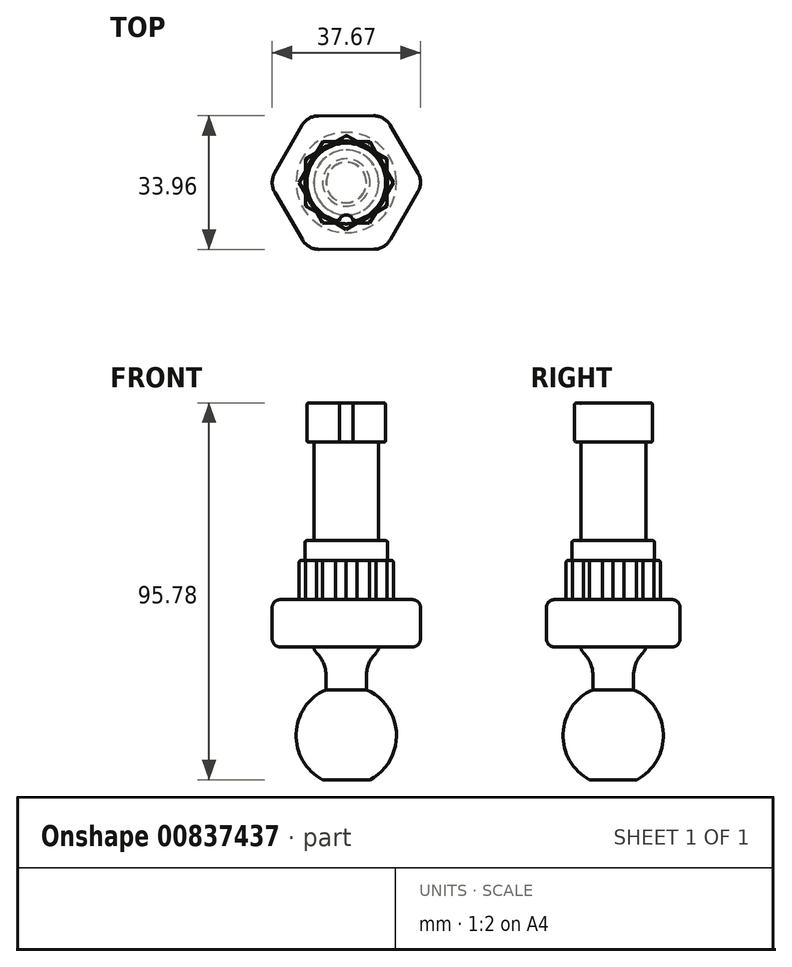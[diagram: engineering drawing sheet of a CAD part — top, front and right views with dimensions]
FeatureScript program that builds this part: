
annotation { "Feature Type Name" : "Feature", "Feature Type Description" : "" }
export const myFeature = defineFeature(function(context is Context, id is Id, definition is map)
    precondition{}
    {
        {
            var Q0;
            Q0=qCreatedBy(makeId("Top.planeOp"),FACE);
            var sketch = newSketch(context, id + "F0", { "sketchPlane" : qUnion([Q0])});
            skCircle(sketch, "E0.cCircle", {"center": v(0, 0) * mm, "radius": 11.95 * mm, "construction": true});
            skLineSegment(sketch, "E0.0", {"start": v(10.36, 5.96) * mm, "end": v(10.36, 2.75) * mm});
            skLineSegment(sketch, "E0.1", {"start": v(10.34, -6) * mm, "end": v(7.56, -7.6) * mm});
            skLineSegment(sketch, "E0.2", {"start": v(-0.02, -11.95) * mm, "end": v(-2.8, -10.34) * mm});
            skLineSegment(sketch, "E0.3", {"start": v(-10.36, -5.96) * mm, "end": v(-10.36, -2.75) * mm});
            skLineSegment(sketch, "E0.4", {"start": v(-10.34, 6) * mm, "end": v(-7.56, 7.6) * mm});
            skLineSegment(sketch, "E0.5", {"start": v(0.02, 11.95) * mm, "end": v(2.8, 10.34) * mm});
            skLineSegment(sketch, "E1", {"start": v(6, 10.34) * mm, "end": v(6.72, 11.59) * mm, "construction": true});
            skLineSegment(sketch, "E2.0", {"start": v(6, 10.34) * mm, "end": v(7.6, 7.56) * mm});
            skLineSegment(sketch, "E2.1", {"start": v(11.95, -0.02) * mm, "end": v(10.34, -2.8) * mm});
            skLineSegment(sketch, "E2.2", {"start": v(5.96, -10.36) * mm, "end": v(2.75, -10.36) * mm});
            skLineSegment(sketch, "E2.3", {"start": v(-6, -10.34) * mm, "end": v(-7.6, -7.56) * mm});
            skLineSegment(sketch, "E2.4", {"start": v(-11.95, 0.02) * mm, "end": v(-10.34, 2.8) * mm});
            skLineSegment(sketch, "E2.5", {"start": v(-5.96, 10.36) * mm, "end": v(-2.75, 10.36) * mm});
            skLineSegment(sketch, "E3.trimOffspring", {"start": v(-7.6, -7.56) * mm, "end": v(-10.36, -5.96) * mm});
            skPoint(sketch, "E4.orphan", {"position": v(-5.2, -8.95) * mm});
            skLineSegment(sketch, "E5.trimOffspring", {"start": v(-10.36, -2.75) * mm, "end": v(-11.95, 0.02) * mm});
            skLineSegment(sketch, "E6.trimOffspring", {"start": v(-2.8, -10.34) * mm, "end": v(-6, -10.34) * mm});
            skLineSegment(sketch, "E7.trimOffspring", {"start": v(2.75, -10.36) * mm, "end": v(-0.02, -11.95) * mm});
            skLineSegment(sketch, "E8.trimOffspring", {"start": v(7.56, -7.6) * mm, "end": v(5.96, -10.36) * mm});
            skLineSegment(sketch, "E9.trimOffspring", {"start": v(-10.34, 2.8) * mm, "end": v(-10.34, 6) * mm});
            skLineSegment(sketch, "E10.trimOffspring", {"start": v(-7.56, 7.6) * mm, "end": v(-5.96, 10.36) * mm});
            skLineSegment(sketch, "E11.trimOffspring", {"start": v(-2.75, 10.36) * mm, "end": v(0.02, 11.95) * mm});
            skLineSegment(sketch, "E12.trimOffspring", {"start": v(2.8, 10.34) * mm, "end": v(6, 10.34) * mm});
            skLineSegment(sketch, "E13.trimOffspring", {"start": v(7.6, 7.56) * mm, "end": v(10.36, 5.96) * mm});
            skPoint(sketch, "E14.orphan", {"position": v(5.2, 8.95) * mm});
            skLineSegment(sketch, "E15.trimOffspring", {"start": v(10.36, 2.75) * mm, "end": v(11.95, -0.02) * mm});
            skLineSegment(sketch, "E16.trimOffspring", {"start": v(10.34, -2.8) * mm, "end": v(10.34, -6) * mm});
            skSolve(sketch);
        }
        {
            var Q0;
            Q0=makeQuery(id+"F0.imprint","IMPRINT",FACE,{"disambiguationData":[TD([[makeQuery(id+"F0.imprint","IMPRINT",EDGE,{"derivedFrom":sQuery(id+"F0.wireOp",EDGE,"E0.0")}),-1.0]])]});
            extrude(context, id + "F1", {"entities" : qUnion([Q0]), "depth" : 10 * mm, "offsetDistance" : 25 * mm});
        }
        {
            var Q0;
            Q0=makeQuery(id+"F1.opExtrude","CAP_FACE",FACE,{"disambiguationData":[OSD([sQuery(id+"F0.wireOp",EDGE,"E0.0"),sQuery(id+"F0.wireOp",EDGE,"E0.1"),sQuery(id+"F0.wireOp",EDGE,"E0.2"),sQuery(id+"F0.wireOp",EDGE,"E0.3"),sQuery(id+"F0.wireOp",EDGE,"E0.4"),sQuery(id+"F0.wireOp",EDGE,"E0.5"),sQuery(id+"F0.wireOp",EDGE,"E2.0"),sQuery(id+"F0.wireOp",EDGE,"E2.1"),sQuery(id+"F0.wireOp",EDGE,"E2.2"),sQuery(id+"F0.wireOp",EDGE,"E2.3"),sQuery(id+"F0.wireOp",EDGE,"E2.4"),sQuery(id+"F0.wireOp",EDGE,"E2.5"),sQuery(id+"F0.wireOp",EDGE,"E3.trimOffspring"),sQuery(id+"F0.wireOp",EDGE,"E5.trimOffspring"),sQuery(id+"F0.wireOp",EDGE,"E6.trimOffspring"),sQuery(id+"F0.wireOp",EDGE,"E7.trimOffspring"),sQuery(id+"F0.wireOp",EDGE,"E8.trimOffspring"),sQuery(id+"F0.wireOp",EDGE,"E9.trimOffspring"),sQuery(id+"F0.wireOp",EDGE,"E10.trimOffspring"),sQuery(id+"F0.wireOp",EDGE,"E11.trimOffspring"),sQuery(id+"F0.wireOp",EDGE,"E12.trimOffspring"),sQuery(id+"F0.wireOp",EDGE,"E13.trimOffspring"),sQuery(id+"F0.wireOp",EDGE,"E15.trimOffspring"),sQuery(id+"F0.wireOp",EDGE,"E16.trimOffspring")])],"isStart":false});
            var sketch = newSketch(context, id + "F2", { "sketchPlane" : qUnion([Q0])});
            skLineSegment(sketch, "E17", {"start": v(-10.36, -2.75) * mm, "end": v(10.36, 2.75) * mm, "construction": true});
            skLineSegment(sketch, "E18", {"start": v(2.75, -10.36) * mm, "end": v(-2.75, 10.36) * mm, "construction": true});
            skCircle(sketch, "E19", {"center": v(0, 0) * mm, "radius": 10.5 * mm});
            skSolve(sketch);
        }
        {
            var Q0;
            Q0=makeQuery(id+"F2.imprint","IMPRINT",FACE,{"disambiguationData":[TD([[makeQuery(id+"F2.imprint","IMPRINT",EDGE,{"derivedFrom":sQuery(id+"F2.wireOp",EDGE,"E19")}),1.0]])]});
            extrude(context, id + "F3", {"entities" : qUnion([Q0]), "operationType" : NewBodyOperationType.ADD, "depth" : 5 * mm, "offsetDistance" : 25 * mm});
        }
        {
            var Q0;
            Q0=makeQuery(id+"F1.opExtrude","CAP_EDGE",EDGE,{"disambiguationData":[OSD([sQuery(id+"F0.wireOp",EDGE,"E2.5")])],"isStart":false});
            var Q1;
            Q1=makeQuery(id+"F1.opExtrude","CAP_EDGE",EDGE,{"disambiguationData":[OSD([sQuery(id+"F0.wireOp",EDGE,"E10.trimOffspring")])],"isStart":false});
            var Q2;
            Q2=makeQuery(id+"F1.opExtrude","CAP_EDGE",EDGE,{"disambiguationData":[OSD([sQuery(id+"F0.wireOp",EDGE,"E0.4")])],"isStart":false});
            var Q3;
            Q3=makeQuery(id+"F1.opExtrude","CAP_EDGE",EDGE,{"disambiguationData":[OSD([sQuery(id+"F0.wireOp",EDGE,"E9.trimOffspring")])],"isStart":false});
            var Q4;
            Q4=makeQuery(id+"F1.opExtrude","CAP_EDGE",EDGE,{"disambiguationData":[OSD([sQuery(id+"F0.wireOp",EDGE,"E2.4")])],"isStart":false});
            var Q5;
            Q5=makeQuery(id+"F1.opExtrude","CAP_EDGE",EDGE,{"disambiguationData":[OSD([sQuery(id+"F0.wireOp",EDGE,"E5.trimOffspring")])],"isStart":false});
            var Q6;
            Q6=makeQuery(id+"F1.opExtrude","CAP_EDGE",EDGE,{"disambiguationData":[OSD([sQuery(id+"F0.wireOp",EDGE,"E0.3")])],"isStart":false});
            var Q7;
            Q7=makeQuery(id+"F1.opExtrude","CAP_EDGE",EDGE,{"disambiguationData":[OSD([sQuery(id+"F0.wireOp",EDGE,"E3.trimOffspring")])],"isStart":false});
            var Q8;
            Q8=makeQuery(id+"F1.opExtrude","CAP_EDGE",EDGE,{"disambiguationData":[OSD([sQuery(id+"F0.wireOp",EDGE,"E2.3")])],"isStart":false});
            var Q9;
            Q9=makeQuery(id+"F1.opExtrude","CAP_EDGE",EDGE,{"disambiguationData":[OSD([sQuery(id+"F0.wireOp",EDGE,"E6.trimOffspring")])],"isStart":false});
            var Q10;
            Q10=makeQuery(id+"F1.opExtrude","CAP_EDGE",EDGE,{"disambiguationData":[OSD([sQuery(id+"F0.wireOp",EDGE,"E0.2")])],"isStart":false});
            var Q11;
            Q11=makeQuery(id+"F1.opExtrude","CAP_EDGE",EDGE,{"disambiguationData":[OSD([sQuery(id+"F0.wireOp",EDGE,"E7.trimOffspring")])],"isStart":false});
            var Q12;
            Q12=makeQuery(id+"F1.opExtrude","CAP_EDGE",EDGE,{"disambiguationData":[OSD([sQuery(id+"F0.wireOp",EDGE,"E2.2")])],"isStart":false});
            var Q13;
            Q13=makeQuery(id+"F1.opExtrude","CAP_EDGE",EDGE,{"disambiguationData":[OSD([sQuery(id+"F0.wireOp",EDGE,"E8.trimOffspring")])],"isStart":false});
            var Q14;
            Q14=makeQuery(id+"F1.opExtrude","CAP_EDGE",EDGE,{"disambiguationData":[OSD([sQuery(id+"F0.wireOp",EDGE,"E0.1")])],"isStart":false});
            var Q15;
            Q15=makeQuery(id+"F1.opExtrude","CAP_EDGE",EDGE,{"disambiguationData":[OSD([sQuery(id+"F0.wireOp",EDGE,"E16.trimOffspring")])],"isStart":false});
            var Q16;
            Q16=makeQuery(id+"F1.opExtrude","CAP_EDGE",EDGE,{"disambiguationData":[OSD([sQuery(id+"F0.wireOp",EDGE,"E2.1")])],"isStart":false});
            var Q17;
            Q17=makeQuery(id+"F1.opExtrude","CAP_EDGE",EDGE,{"disambiguationData":[OSD([sQuery(id+"F0.wireOp",EDGE,"E15.trimOffspring")])],"isStart":false});
            var Q18;
            Q18=makeQuery(id+"F1.opExtrude","CAP_EDGE",EDGE,{"disambiguationData":[OSD([sQuery(id+"F0.wireOp",EDGE,"E0.0")])],"isStart":false});
            var Q19;
            Q19=makeQuery(id+"F1.opExtrude","CAP_EDGE",EDGE,{"disambiguationData":[OSD([sQuery(id+"F0.wireOp",EDGE,"E13.trimOffspring")])],"isStart":false});
            var Q20;
            Q20=makeQuery(id+"F1.opExtrude","CAP_EDGE",EDGE,{"disambiguationData":[OSD([sQuery(id+"F0.wireOp",EDGE,"E2.0")])],"isStart":false});
            var Q21;
            Q21=makeQuery(id+"F1.opExtrude","CAP_EDGE",EDGE,{"disambiguationData":[OSD([sQuery(id+"F0.wireOp",EDGE,"E12.trimOffspring")])],"isStart":false});
            var Q22;
            Q22=makeQuery(id+"F1.opExtrude","CAP_EDGE",EDGE,{"disambiguationData":[OSD([sQuery(id+"F0.wireOp",EDGE,"E0.5")])],"isStart":false});
            var Q23;
            Q23=makeQuery(id+"F1.opExtrude","CAP_EDGE",EDGE,{"disambiguationData":[OSD([sQuery(id+"F0.wireOp",EDGE,"E11.trimOffspring")])],"isStart":false});
            fillet(context, id + "F4", {"entities" : qUnion([Q0, Q1, Q2, Q3, Q4, Q5, Q6, Q7, Q8, Q9, Q10, Q11, Q12, Q13, Q14, Q15, Q16, Q17, Q18, Q19, Q20, Q21, Q22, Q23]), "radius" : .5 * mm, "tangentPropagation" : true, "allowEdgeOverflow" : false});
        }
        {
            var Q0;
            Q0=makeQuery(id+"F3.opExtrude","CAP_FACE",FACE,{"disambiguationData":[OSD([sQuery(id+"F2.wireOp",EDGE,"E19")])],"isStart":false});
            var sketch = newSketch(context, id + "F5", { "sketchPlane" : qUnion([Q0])});
            skCircle(sketch, "E20", {"center": v(0, 0) * mm, "radius": 8.25 * mm});
            skSolve(sketch);
        }
        {
            var Q0;
            Q0=makeQuery(id+"F5.imprint","IMPRINT",FACE,{"disambiguationData":[TD([[makeQuery(id+"F5.imprint","IMPRINT",EDGE,{"derivedFrom":sQuery(id+"F5.wireOp",EDGE,"E20")}),1.0]])]});
            extrude(context, id + "F6", {"entities" : qUnion([Q0]), "operationType" : NewBodyOperationType.ADD, "depth" : 25 * mm, "offsetDistance" : 25 * mm});
        }
        {
            var Q0;
            Q0=makeQuery(id+"F6.opExtrude","CAP_FACE",FACE,{"disambiguationData":[OSD([sQuery(id+"F5.wireOp",EDGE,"E20")])],"isStart":false});
            var sketch = newSketch(context, id + "F7", { "sketchPlane" : qUnion([Q0])});
            skCircle(sketch, "E21", {"center": v(0, 0) * mm, "radius": 10 * mm});
            skSolve(sketch);
        }
        {
            var Q0;
            Q0=makeQuery(id+"F7.imprint","IMPRINT",FACE,{"disambiguationData":[TD([[makeQuery(id+"F7.imprint","IMPRINT",EDGE,{"derivedFrom":sQuery(id+"F7.wireOp",EDGE,"E21")}),1.0]])]});
            var Q1;
            Q1=makeQuery(id+"F7.imprint","IMPRINT",FACE,{"disambiguationData":[TD([[makeQuery(id+"F7.imprint","IMPRINT",EDGE,{"derivedFrom":makeQuery(id+"F6.opExtrude","CAP_EDGE",EDGE,{"disambiguationData":[OSD([sQuery(id+"F5.wireOp",EDGE,"E20")])],"isStart":false})}),1.0]])]});
            extrude(context, id + "F8", {"entities" : qUnion([Q0, Q1]), "operationType" : NewBodyOperationType.ADD, "depth" : 10 * mm, "offsetDistance" : 25 * mm});
        }
        {
            var Q0;
            Q0=makeQuery(id+"F8.opExtrude","CAP_FACE",FACE,{"disambiguationData":[OSD([sQuery(id+"F7.wireOp",EDGE,"E21")])],"isStart":true});
            var sketch = newSketch(context, id + "F9", { "sketchPlane" : qUnion([Q0])});
            skLineSegment(sketch, "E22", {"start": v(0, 10) * mm, "end": v(0, 8.25) * mm, "construction": true});
            skArc(sketch, "E23", {"start": v(0, 8.25) * mm, "mid": v(1.18, 8.7) * mm, "end": v(1.74, 9.85) * mm});
            skArc(sketch, "E24", {"start": v(0, 8.25) * mm, "mid": v(-1.18, 8.7) * mm, "end": v(-1.74, 9.85) * mm});
            skSolve(sketch);
        }
        {
            var Q0;
            {var subQ0=sQuery(id+"F9.wireOp",EDGE,"E23");Q0=makeQuery(id+"F9.imprint","IMPRINT",FACE,{"disambiguationData":[TD([[makeQuery(id+"F9.imprint","IMPRINT",EDGE,{"derivedFrom":subQ0}),1.0]])]});}
            extrude(context, id + "F10", {"entities" : qUnion([Q0]), "operationType" : NewBodyOperationType.REMOVE, "oppositeDirection" : true, "depth" : 25 * mm, "offsetDistance" : 25 * mm});
        }
        {
            var Q0;
            Q0=makeQuery(id+"F8.opExtrude","CAP_EDGE",EDGE,{"disambiguationData":[OSD([sQuery(id+"F7.wireOp",EDGE,"E21")])],"isStart":false});
            var Q1;
            Q1=makeQuery(id+"F10.boolean.opBoolean","INTERSECT",EDGE,{"derivedFrom":[makeQuery(id+"F8.opExtrude","CAP_FACE",FACE,{"disambiguationData":[OSD([sQuery(id+"F7.wireOp",EDGE,"E21")])],"isStart":false}),makeQuery(id+"F10.opExtrude","SWEPT_FACE",FACE,{"disambiguationData":[OSD([sQuery(id+"F9.wireOp",EDGE,"E23"),sQuery(id+"F9.wireOp",EDGE,"E24")])]})]});
            var Q2;
            Q2=makeQuery(id+"F10.boolean.opBoolean","COPY",EDGE,{"derivedFrom":makeQuery(id+"F10.opExtrude","SWEPT_EDGE",EDGE,{"disambiguationData":[OSD([sQuery(id+"F7.wireOp",EDGE,"E21"),sQuery(id+"F9.wireOp",EDGE,"E24")])]})});
            var Q3;
            Q3=makeQuery(id+"F10.boolean.opBoolean","COPY",EDGE,{"derivedFrom":makeQuery(id+"F10.opExtrude","SWEPT_EDGE",EDGE,{"disambiguationData":[OSD([sQuery(id+"F7.wireOp",EDGE,"E21"),sQuery(id+"F9.wireOp",EDGE,"E23")])]})});
            var Q4;
            Q4=makeQuery(id+"F8.opExtrude","CAP_EDGE",EDGE,{"disambiguationData":[OSD([sQuery(id+"F7.wireOp",EDGE,"E21")])],"isStart":true});
            var Q5;
            Q5=makeQuery(id+"F10.boolean.opBoolean","COPY",EDGE,{"disambiguationData":[OD(1.0)],"derivedFrom":makeQuery(id+"F10.opExtrude","CAP_EDGE",EDGE,{"disambiguationData":[OSD([sQuery(id+"F9.wireOp",EDGE,"E23"),sQuery(id+"F9.wireOp",EDGE,"E24")])],"isStart":true})});
            var Q6;
            Q6=makeQuery(id+"F10.boolean.opBoolean","COPY",EDGE,{"disambiguationData":[OD(0.0)],"derivedFrom":makeQuery(id+"F10.opExtrude","CAP_EDGE",EDGE,{"disambiguationData":[OSD([sQuery(id+"F9.wireOp",EDGE,"E23"),sQuery(id+"F9.wireOp",EDGE,"E24")])],"isStart":true})});
            fillet(context, id + "F11", {"entities" : qUnion([Q0, Q1, Q2, Q3, Q4, Q5, Q6]), "radius" : .5 * mm, "tangentPropagation" : true, "allowEdgeOverflow" : false});
        }
        {
            var Q0;
            Q0=makeQuery(id+"F6.opExtrude","CAP_EDGE",EDGE,{"disambiguationData":[OSD([sQuery(id+"F5.wireOp",EDGE,"E20")])],"isStart":true});
            var Q1;
            Q1=makeQuery(id+"F3.opExtrude","CAP_EDGE",EDGE,{"disambiguationData":[OSD([sQuery(id+"F2.wireOp",EDGE,"E19")])],"isStart":false});
            fillet(context, id + "F12", {"entities" : qUnion([Q0, Q1]), "radius" : .5 * mm, "tangentPropagation" : true, "allowEdgeOverflow" : false});
        }
        {
            var Q0;
            Q0=makeQuery(id+"F1.opExtrude","CAP_FACE",FACE,{"disambiguationData":[OSD([sQuery(id+"F0.wireOp",EDGE,"E0.0"),sQuery(id+"F0.wireOp",EDGE,"E0.1"),sQuery(id+"F0.wireOp",EDGE,"E0.2"),sQuery(id+"F0.wireOp",EDGE,"E0.3"),sQuery(id+"F0.wireOp",EDGE,"E0.4"),sQuery(id+"F0.wireOp",EDGE,"E0.5"),sQuery(id+"F0.wireOp",EDGE,"E2.0"),sQuery(id+"F0.wireOp",EDGE,"E2.1"),sQuery(id+"F0.wireOp",EDGE,"E2.2"),sQuery(id+"F0.wireOp",EDGE,"E2.3"),sQuery(id+"F0.wireOp",EDGE,"E2.4"),sQuery(id+"F0.wireOp",EDGE,"E2.5"),sQuery(id+"F0.wireOp",EDGE,"E3.trimOffspring"),sQuery(id+"F0.wireOp",EDGE,"E5.trimOffspring"),sQuery(id+"F0.wireOp",EDGE,"E6.trimOffspring"),sQuery(id+"F0.wireOp",EDGE,"E7.trimOffspring"),sQuery(id+"F0.wireOp",EDGE,"E8.trimOffspring"),sQuery(id+"F0.wireOp",EDGE,"E9.trimOffspring"),sQuery(id+"F0.wireOp",EDGE,"E10.trimOffspring"),sQuery(id+"F0.wireOp",EDGE,"E11.trimOffspring"),sQuery(id+"F0.wireOp",EDGE,"E12.trimOffspring"),sQuery(id+"F0.wireOp",EDGE,"E13.trimOffspring"),sQuery(id+"F0.wireOp",EDGE,"E15.trimOffspring"),sQuery(id+"F0.wireOp",EDGE,"E16.trimOffspring")])],"isStart":true});
            var sketch = newSketch(context, id + "F13", { "sketchPlane" : qUnion([Q0])});
            skCircle(sketch, "E25.cCircle", {"center": v(0, 0) * mm, "radius": 16.96 * mm, "construction": true});
            skLineSegment(sketch, "E25.0", {"start": v(-11.22, -14.53) * mm, "end": v(-18.17, -2.4) * mm});
            skLineSegment(sketch, "E25.1", {"start": v(-18.16, 2.5) * mm, "end": v(-11.17, 14.54) * mm});
            skLineSegment(sketch, "E25.2", {"start": v(-6.92, 16.98) * mm, "end": v(7.06, 16.94) * mm});
            skLineSegment(sketch, "E25.3", {"start": v(11.22, 14.53) * mm, "end": v(18.2, 2.35) * mm});
            skLineSegment(sketch, "E25.4", {"start": v(18.2, -2.45) * mm, "end": v(11.17, -14.54) * mm});
            skLineSegment(sketch, "E25.5", {"start": v(6.92, -16.98) * mm, "end": v(-7.06, -16.94) * mm});
            skPoint(sketch, "E25.0.midPoint", {"position": v(-14.7, -8.44) * mm});
            skPoint(sketch, "E26.visualSharp", {"position": v(9.75, -16.99) * mm});
            skArc(sketch, "E26.filletArc", {"start": v(6.92, -16.98) * mm, "mid": v(9.37, -16.33) * mm, "end": v(11.17, -14.54) * mm});
            skPoint(sketch, "E27.visualSharp", {"position": v(-9.84, -16.93) * mm});
            skArc(sketch, "E27.filletArc", {"start": v(-11.22, -14.53) * mm, "mid": v(-9.46, -16.3) * mm, "end": v(-7.06, -16.94) * mm});
            skPoint(sketch, "E28.visualSharp", {"position": v(-19.58, 0.05) * mm});
            skArc(sketch, "E28.filletArc", {"start": v(-18.16, 2.5) * mm, "mid": v(-18.82, 0.05) * mm, "end": v(-18.17, -2.4) * mm});
            skPoint(sketch, "E29.visualSharp", {"position": v(-9.75, 16.99) * mm});
            skArc(sketch, "E29.filletArc", {"start": v(-6.92, 16.98) * mm, "mid": v(-9.37, 16.33) * mm, "end": v(-11.17, 14.54) * mm});
            skPoint(sketch, "E30.visualSharp", {"position": v(9.84, 16.93) * mm});
            skArc(sketch, "E30.filletArc", {"start": v(11.22, 14.53) * mm, "mid": v(9.46, 16.3) * mm, "end": v(7.06, 16.94) * mm});
            skPoint(sketch, "E31.visualSharp", {"position": v(19.58, -0.05) * mm});
            skArc(sketch, "E31.filletArc", {"start": v(18.2, -2.45) * mm, "mid": v(18.84, -0.05) * mm, "end": v(18.2, 2.35) * mm});
            skSolve(sketch);
        }
        {
            var Q0;
            Q0=makeQuery(id+"F13.imprint","IMPRINT",FACE,{"disambiguationData":[TD([[makeQuery(id+"F13.imprint","IMPRINT",EDGE,{"derivedFrom":sQuery(id+"F13.wireOp",EDGE,"XwkZxwQT-tXsu-qyU6-IrZG-78iqKTn2pKXx")}),1.0]])]});
            var Q1;
            Q1=makeQuery(id+"F13.imprint","IMPRINT",FACE,{"disambiguationData":[TD([[makeQuery(id+"F13.imprint","IMPRINT",EDGE,{"derivedFrom":makeQuery(id+"F1.opExtrude","CAP_EDGE",EDGE,{"disambiguationData":[OSD([sQuery(id+"F0.wireOp",EDGE,"E0.0")])],"isStart":true})}),1.0]])]});
            var Q2;
            Q2=makeQuery(id+"F13.imprint","IMPRINT",FACE,{"disambiguationData":[TD([[makeQuery(id+"F13.imprint","IMPRINT",EDGE,{"derivedFrom":sQuery(id+"F13.wireOp",EDGE,"E25.0")}),-1.0]])]});
            extrude(context, id + "F14", {"entities" : qUnion([Q0, Q1, Q2]), "operationType" : NewBodyOperationType.ADD, "depth" : 12 * mm, "offsetDistance" : 25 * mm});
        }
        {
            var Q0;
            Q0=makeQuery(id+"F14.opExtrude","CAP_EDGE",EDGE,{"disambiguationData":[OSD([sQuery(id+"F13.wireOp",EDGE,"XwkZxwQT-tXsu-qyU6-IrZG-78iqKTn2pKXx")])],"isStart":false});
            var Q1;
            Q1=makeQuery(id+"F14.opExtrude","CAP_EDGE",EDGE,{"disambiguationData":[OSD([sQuery(id+"F13.wireOp",EDGE,"XwkZxwQT-tXsu-qyU6-IrZG-78iqKTn2pKXx")])],"isStart":true});
            var Q2;
            Q2=makeQuery(id+"F14.opExtrude","CAP_EDGE",EDGE,{"disambiguationData":[OSD([sQuery(id+"F13.wireOp",EDGE,"E25.3")])],"isStart":false});
            var Q3;
            Q3=makeQuery(id+"F14.opExtrude","CAP_EDGE",EDGE,{"disambiguationData":[OSD([sQuery(id+"F13.wireOp",EDGE,"E25.3")])],"isStart":true});
            fillet(context, id + "F15", {"entities" : qUnion([Q0, Q1, Q2, Q3]), "radius" : 2 * mm, "tangentPropagation" : true, "allowEdgeOverflow" : false});
        }
        {
            var Q0;
            Q0=qCreatedBy(makeId("Right.planeOp"),FACE);
            var sketch = newSketch(context, id + "F16", { "sketchPlane" : qUnion([Q0])});
            skLineSegment(sketch, "E32", {"start": v(0, 0) * mm, "end": v(0, -51.37) * mm});
            skLineSegment(sketch, "E33", {"start": v(0, -10.99) * mm, "end": v(8.28, -10.99) * mm});
            skLineSegment(sketch, "E34", {"start": v(8.28, -10.99) * mm, "end": v(8.28, -12.78) * mm});
            skArc(sketch, "E35", {"start": v(6.02, -45.78) * mm, "mid": v(12.74, -34.07) * mm, "end": v(5.18, -22.89) * mm});
            skFitSpline(sketch, "E36", {"points": [v(8.28, -12.78) * mm, v(5.65, -16.42) * mm, v(5.18, -22.89) * mm], "startDerivative": vector(-6.91, -7.13) * mm, "endDerivative": vector(0.46, -12.91) * mm});
            skLineSegment(sketch, "E37", {"start": v(6.02, -45.78) * mm, "end": v(0, -45.78) * mm});
            skPoint(sketch, "E38.orphan", {"position": v(0, -47.29) * mm});
            skSolve(sketch);
        }
        {
            var Q0;
            {var subQ1=sQuery(id+"F16.wireOp",EDGE,"E33");Q0=makeQuery(id+"F16.imprint","IMPRINT",FACE,{"disambiguationData":[TD([[makeQuery(id+"F16.imprint","IMPRINT",EDGE,{"derivedFrom":subQ1}),-1.0]])]});}
            var Q1;
            Q1=sQuery(id+"F16.wireOp",EDGE,"E32");
            revolve(context, id + "F17", {"operationType" : NewBodyOperationType.ADD, "surfaceOperationType" : NewSurfaceOperationType.NEW, "entities" : qUnion([Q0]), "axis" : qUnion([Q1]), "revolveType" : RevolveType.FULL});
        }
        {
            var Q0;
            Q0=makeQuery(id+"F17.opRevolve","SWEPT_EDGE",EDGE,{"disambiguationData":[OSD([sQuery(id+"F16.wireOp",EDGE,"E34"),sQuery(id+"F16.wireOp",EDGE,"E36")])]});
            fillet(context, id + "F18", {"entities" : qUnion([Q0]), "radius" : 3 * mm, "tangentPropagation" : true, "allowEdgeOverflow" : false});
        }
    });
